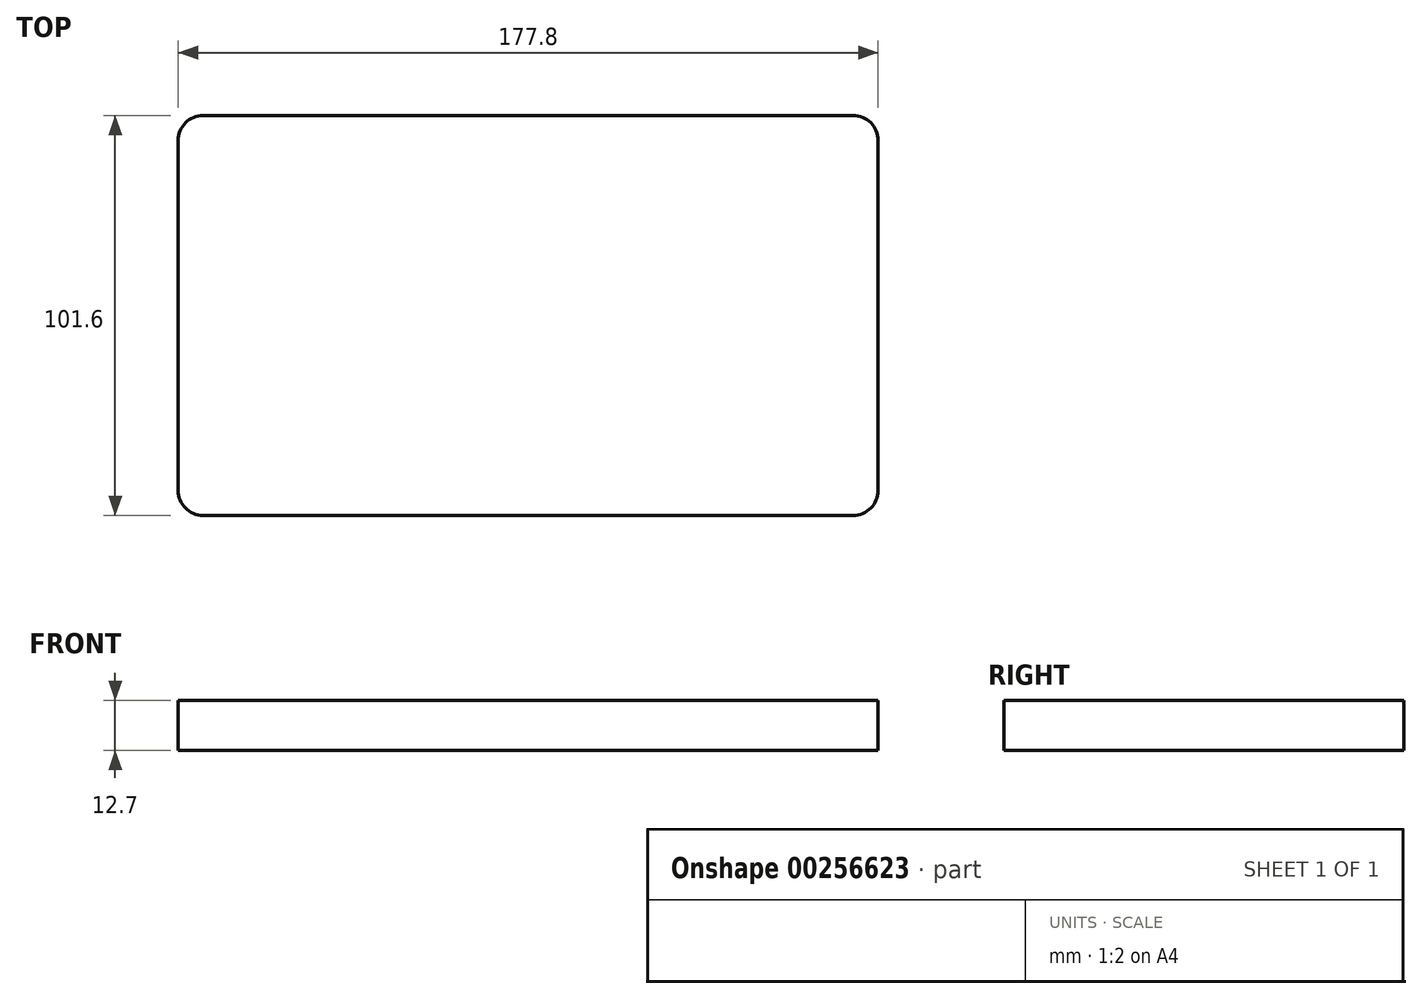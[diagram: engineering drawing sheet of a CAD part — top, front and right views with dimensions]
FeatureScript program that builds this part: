
annotation { "Feature Type Name" : "Feature", "Feature Type Description" : "" }
export const myFeature = defineFeature(function(context is Context, id is Id, definition is map)
    precondition{}
    {
        {
            var Q0;
            Q0=qCreatedBy(makeId("Top.planeOp"),FACE);
            var sketch = newSketch(context, id + "F0", { "sketchPlane" : qUnion([Q0])});
            skLineSegment(sketch, "E0.bottom", {"start": v(-82.55, -50.8) * mm, "end": v(82.55, -50.8) * mm});
            skLineSegment(sketch, "E0.top", {"start": v(-82.55, 50.8) * mm, "end": v(82.55, 50.8) * mm});
            skLineSegment(sketch, "E0.left", {"start": v(-88.9, -44.45) * mm, "end": v(-88.9, 44.45) * mm});
            skLineSegment(sketch, "E0.right", {"start": v(88.9, -44.45) * mm, "end": v(88.9, 44.45) * mm});
            skPoint(sketch, "E0.middle", {"position": v(0, 0) * mm});
            skPoint(sketch, "E1.visualSharp", {"position": v(-88.9, 50.8) * mm});
            skArc(sketch, "E1.filletArc", {"start": v(-82.55, 50.8) * mm, "mid": v(-87.04, 48.94) * mm, "end": v(-88.9, 44.45) * mm});
            skPoint(sketch, "E2.visualSharp", {"position": v(88.9, 50.8) * mm});
            skArc(sketch, "E2.filletArc", {"start": v(88.9, 44.45) * mm, "mid": v(87.04, 48.94) * mm, "end": v(82.55, 50.8) * mm});
            skPoint(sketch, "E3.visualSharp", {"position": v(88.9, -50.8) * mm});
            skArc(sketch, "E3.filletArc", {"start": v(82.55, -50.8) * mm, "mid": v(87.04, -48.94) * mm, "end": v(88.9, -44.45) * mm});
            skPoint(sketch, "E4.visualSharp", {"position": v(-88.9, -50.8) * mm});
            skArc(sketch, "E4.filletArc", {"start": v(-88.9, -44.45) * mm, "mid": v(-87.04, -48.94) * mm, "end": v(-82.55, -50.8) * mm});
            skSolve(sketch);
        }
        {
            var Q0;
            Q0=makeQuery(id+"F0.imprint","IMPRINT",FACE,{"disambiguationData":[TD([[makeQuery(id+"F0.imprint","IMPRINT",EDGE,{"derivedFrom":sQuery(id+"F0.wireOp",EDGE,"E0.bottom")}),1.0]])]});
            extrude(context, id + "F1", {"entities" : qUnion([Q0]), "endBound" : BoundingType.SYMMETRIC, "depth" : 12.7 * mm});
        }
    });
